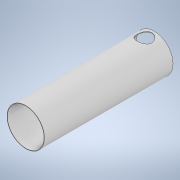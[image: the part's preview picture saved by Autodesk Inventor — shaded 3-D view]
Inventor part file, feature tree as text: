
AUTODESK INVENTOR PART (.ipt)
format: ipt  version: 2021 (Build 250183000, 183)  size: 113,664 bytes
history: native  units: mm
features: extrude x2, sketch x2
ambient origin geometry x8: Origin, YZ Plane, XZ Plane, XY Plane, X Axis, Y Axis, Z Axis, Center Point
bodies: Solid1 (feature_tree)
feature tree (4):
  extrude  "Extrusion1"  Depth=38.0mm
  extrude  "Extrusion2"  Depth=10.0mm
  sketch  "Sketch1"  dims[d0=37.0mm d1=38.0mm]
  sketch  "Sketch2"  dims[d2=130.0mm d3=0.0mm d4=15.0mm d5=10.0mm d6=130.0mm d7=0.0mm]
